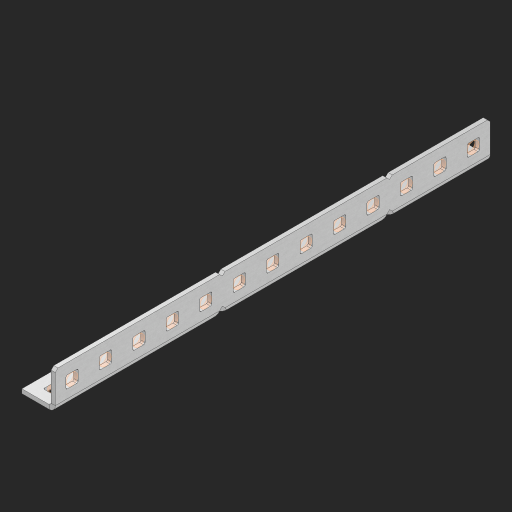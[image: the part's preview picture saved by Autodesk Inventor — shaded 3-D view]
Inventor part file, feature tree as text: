
AUTODESK INVENTOR PART (.ipt)
format: ipt  version: 2023 (Build 270158000, 158)  size: 557,056 bytes
history: native  units: in
note: dims shown in document units (in); Inventor stores cm internally (conversion verified against a paired STEP export)
features: other x31, extrude x25, sheet_metal_op x10, sketch x8, mirror x1, pattern_linear x1, chamfer x1
ambient origin geometry x8: Origin, YZ Plane, XZ Plane, XY Plane, X Axis, Y Axis, Z Axis, Center Point
bodies: Solid1 (feature_tree), Body (feature_tree)
feature tree (77):
  other  "Flange Pattern Plane"
  sheet_metal_op  "Flange Pattern"
  sheet_metal_op  "Body Pattern"
  other  "Arc Length"
  mirror  "Notch Mirror"
  pattern_linear  "Notch Pattern"  Spacing1=0.25in  [1 undecoded]
  chamfer  "End Chamfer"
  extrude  "Half Cut"  Depth=0.0625in
  sketch  "Sketch1"  dims[d0=1.5in]
  other  "Plate1"
  sketch  "Sketch2"  dims[d1=6.5in]
  other  "Plate2"
  sheet_metal_op  "Bend1"
  sheet_metal_op  "Corner1"
  sketch  "Sketch3"  dims[d2=0.0625in]
  other  "Flange Pattern Sketch"
  sketch  "Sketch7"  dims[d3=0.0625in]
  other  "Srf1"
  other  "Srf2"
  sketch  "Sketch8"  dims[d4=0.0312in]
  sketch  "Sketch9"  dims[d5=0.125in]
  other  "Srf91"
  sheet_metal_op  "Body Pattern Sketch"
  other  "Srf92"
  sketch  "Sketch13"  dims[d6=0.0625in]
  sketch  "Sketch14"  dims[d7=0.5in d8=90.0deg d9=0.0312in d10=0.25in d11=0.0625in d12=0.0625in d16=0.182in d17=0.02in d18=0.0625in d19=0.0in d20=0.25in d21=0.25in d46=0.172in d47=1.0in d48=0.0in d49=0.182in d50=0.02in d51=0.25in d52=0.25in d53=0.0625in d54=0.0in d55=0.172in d56=1.0in d57=0.0in d60=5.1181in d62=0.5in d63=0.3937in d65=0.5in d85=0.1473in d86=0.1782in d88=0.04in d89=0.0625in d90=0.0in d91=0.04in d92=0.0491in d95=2.5in d96=0.04in d97=0.25in d98=45.0deg d101=0.0in d102=2.497in d131=0.5in d132=5.1181in d134=0.5in d139=0.5in]
  other  "Srf856"
  other  "Srf1310"
  other  "Srf1311"
  other  "Srf1312"
  other  "Srf1376"
  other  "Srf1377"
  other  "Srf1728"
  other  "Srf1755"
  other  "Srf1878"
  other  "Srf1879"
  other  "Srf1880"
  other  "Srf1881"
  other  "Srf1882"
  other  "Srf1883"
  other  "Srf1884"
  other  "Srf1942"
  other  "Srf1943"
  other  "Srf1944"
  other  "Srf1945"
  other  "Srf1946"
  other  "Srf1947"
  other  "Srf1948"
  sheet_metal_op  "Flange Stamp"
  sheet_metal_op  "Flange Circle"
  sheet_metal_op  "Body Stamp"
  sheet_metal_op  "Body Circle"
  sheet_metal_op  "Notch"
  extrude  "ExtrusionSrf2"  Depth=0.0625in
  extrude  "ExtrusionSrf92"  Depth=0.5in
  extrude  "ExtrusionSrf856"  Depth=0.02in
  extrude  "ExtrusionSrf1310"  Depth=0.0625in
  extrude  "ExtrusionSrf1311"  TaperAngle=0.0deg  [1 undecoded]
  extrude  "ExtrusionSrf1312"  Depth=0.5in
  extrude  "ExtrusionSrf1376"  Depth=0.5in
  extrude  "ExtrusionSrf1377"  Depth=0.5in
  extrude  "ExtrusionSrf1728"  Depth=0.5in TaperAngle=0.0deg
  extrude  "ExtrusionSrf1755"  Depth=0.5in
  extrude  "ExtrusionSrf1878"  Depth=0.02in
  extrude  "ExtrusionSrf1879"  Depth=0.5in
  extrude  "ExtrusionSrf1880"  Depth=0.5in
  extrude  "ExtrusionSrf1881"  Depth=0.0625in
  extrude  "ExtrusionSrf1882"  TaperAngle=0.0deg  [1 undecoded]
  extrude  "ExtrusionSrf1883"  Depth=0.5in
  extrude  "ExtrusionSrf1884"  Depth=0.5in TaperAngle=0.0deg
  extrude  "ExtrusionSrf1942"  Depth=0.5in
  extrude  "ExtrusionSrf1943"  Depth=0.5in
  extrude  "ExtrusionSrf1944"  Depth=0.5in
  extrude  "ExtrusionSrf1945"  Depth=0.5in
  extrude  "ExtrusionSrf1946"  Depth=0.5in
  extrude  "ExtrusionSrf1947"  Depth=0.0625in
  extrude  "ExtrusionSrf1948"  TaperAngle=0.0deg  [1 undecoded]
note: 4 required parameter values undecoded (feature->parameter linkage not recoverable at this tier; creation-order binding heuristic only, values carry confidence <= 0.55)
